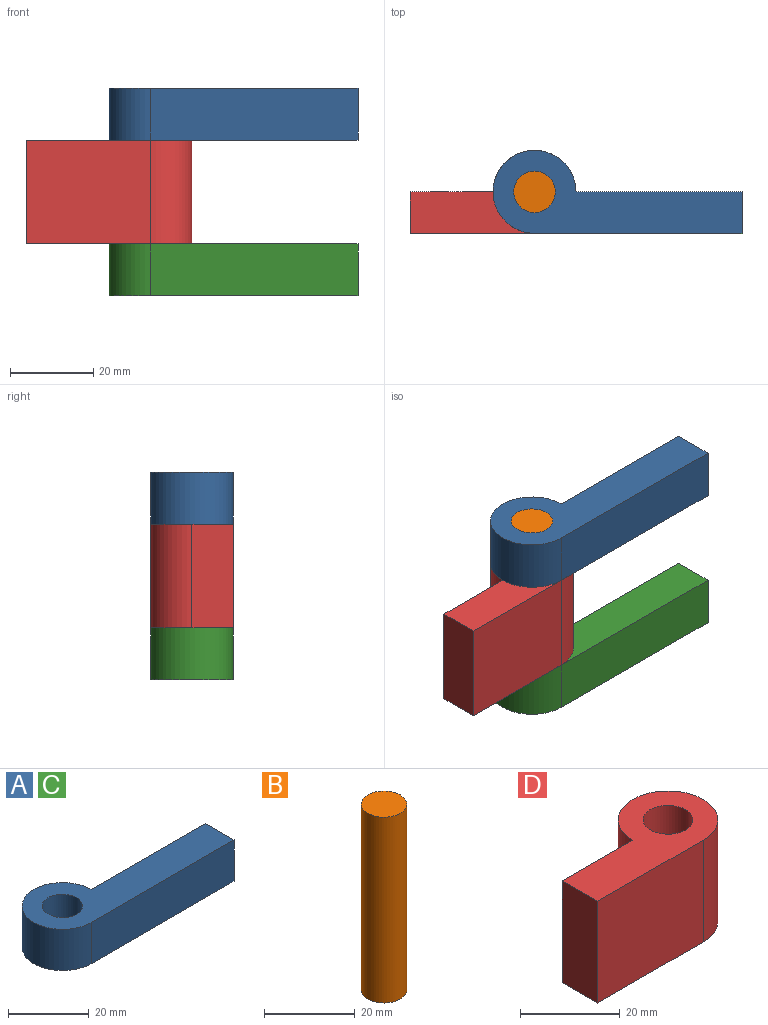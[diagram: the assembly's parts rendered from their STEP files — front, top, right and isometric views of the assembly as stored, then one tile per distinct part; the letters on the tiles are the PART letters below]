
ASSEMBLY  parts=4 mates=7
PART A: 7 faces, bbox 60x20x12.5 mm
  f0: plane 40x12.5mm, normal (0,1,0), area 500mm2, adj f1,f3,f5,f6
  f1: cylinder r=10mm len=20mm, axis (0,0,1), area 589mm2, adj f0,f2,f5,f6
  f2: plane 50x12.5mm, normal (0,-1,0), area 625mm2, adj f1,f3,f5,f6
  f3: plane 12.5x10mm, normal (1,0,0), area 125mm2, adj f0,f2,f5,f6
  f4: cylinder r=5mm len=12.5mm, axis (0,0,1), area 392.7mm2, adj f5,f6
  f5: plane 60x20mm, normal (0,0,-1), area 657.1mm2, adj f0,f1,f2,f3,f4
  f6: plane 60x20mm, normal (0,0,1), area 657.1mm2, adj f0,f1,f2,f3,f4
PART B: 3 faces, bbox 10x10x50 mm
  f0: plane 10x10mm, normal (0,0,1), area 78.5mm2, adj f1
  f1: cylinder r=5mm len=50mm, axis (0,0,-1), area 1570.8mm2, adj f0,f2
  f2: plane 10x10mm, normal (0,0,-1), area 78.5mm2, adj f1
PART C: same geometry as A
PART D: 7 faces, bbox 40x20x25 mm
  f0: plane 30x25mm, normal (0,-1,0), area 750mm2, adj f1,f3,f5,f6
  f1: cylinder r=10mm len=25mm, axis (0,0,-1), area 1178.1mm2, adj f0,f2,f5,f6
  f2: plane 25x20mm, normal (0,1,0), area 500mm2, adj f1,f3,f5,f6
  f3: plane 25x10mm, normal (-1,0,0), area 250mm2, adj f0,f2,f5,f6
  f4: cylinder r=5mm len=25mm, axis (0,0,-1), area 785.4mm2, adj f5,f6
  f5: plane 40x20mm, normal (0,0,1), area 457.1mm2, adj f0,f1,f2,f3,f4
  f6: plane 40x20mm, normal (0,0,-1), area 457.1mm2, adj f0,f1,f2,f3,f4
PLACE A t=(-7.99,9.51,35.1)mm
PLACE B t=(-7.99,9.51,-2.4)mm
PLACE C t=(-7.99,9.51,-2.4)mm
PLACE D t=(-7.99,9.51,-2.4)mm
MATE planar C.f6 <-> D.f6  axis (0,0,1) through (10.53,6.21,-2.4)mm
MATE cylindrical B.f1 <-> D.f1  axis (0,0,-1) through (-7.99,9.51,10.1)mm
MATE cylindrical A.f1 <-> D.f1  axis (0,0,1) through (-7.99,9.51,28.85)mm
MATE planar B.f1 <-> C.f5  axis (0,0,-1) through (-7.99,9.51,-14.9)mm
MATE planar A.f0 <-> C.f0  axis (0,1,0) through (42.01,9.51,22.6)mm
MATE planar A.f5 <-> D.f5  axis (0,0,-1) through (10.53,6.21,22.6)mm
MATE cylindrical C.f1 <-> D.f1  axis (0,0,1) through (-7.99,9.51,-8.65)mm
